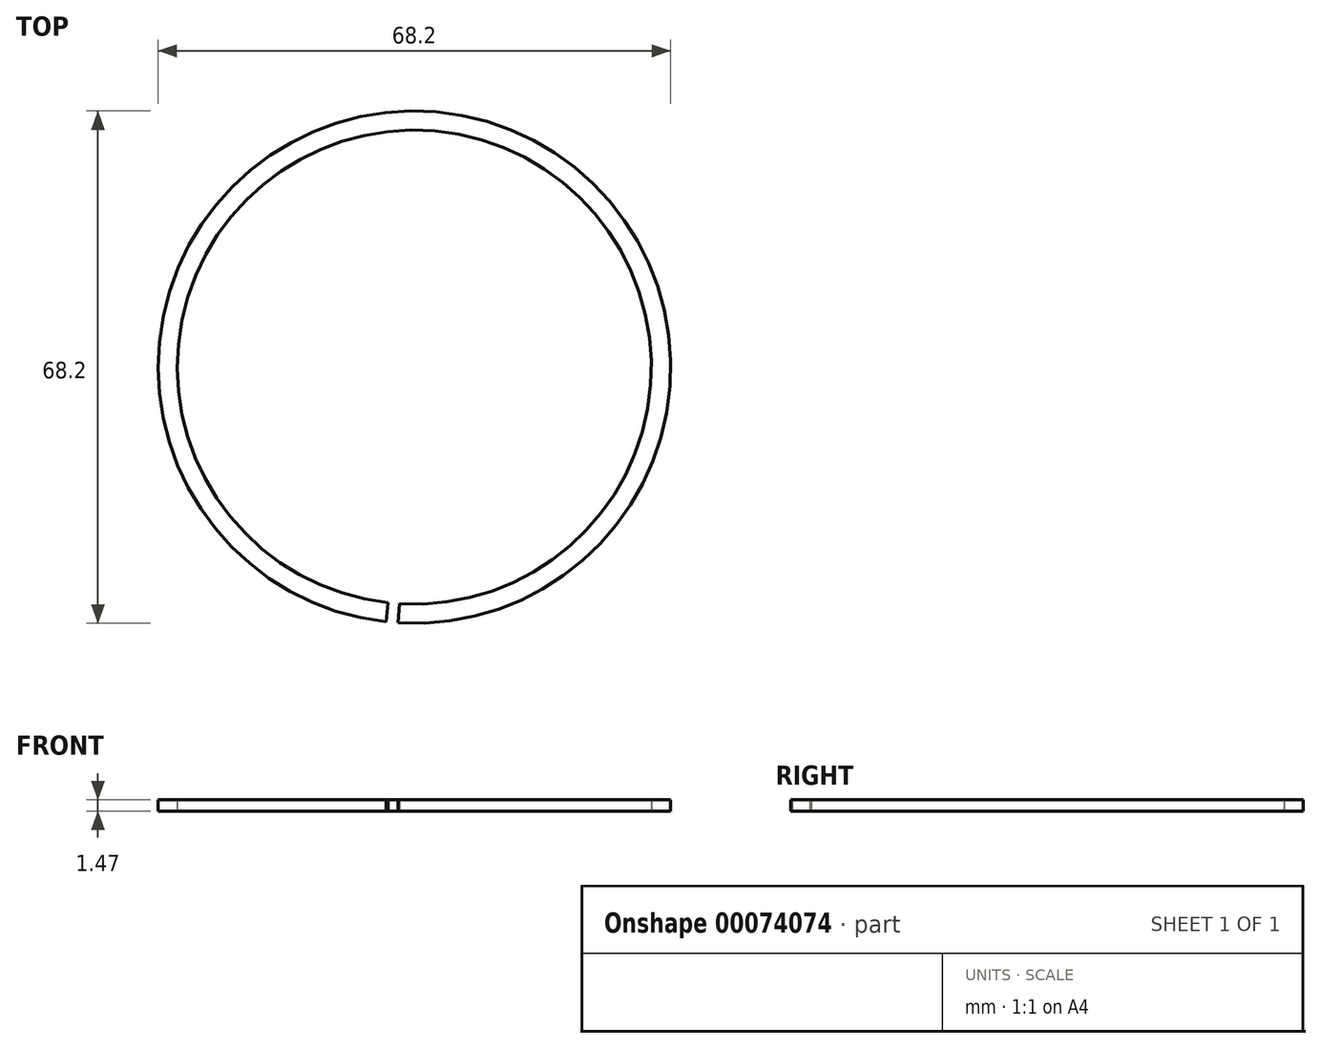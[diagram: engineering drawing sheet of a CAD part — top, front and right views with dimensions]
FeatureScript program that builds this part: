
annotation { "Feature Type Name" : "Feature", "Feature Type Description" : "" }
export const myFeature = defineFeature(function(context is Context, id is Id, definition is map)
    precondition{}
    {
        {
            var Q0;
            Q0=qCreatedBy(makeId("Top.planeOp"),FACE);
            var sketch = newSketch(context, id + "F0", { "sketchPlane" : qUnion([Q0])});
            skArc(sketch, "E0", {"start": v(-2.15, -34.03) * mm, "mid": v(2.95, 33.97) * mm, "end": v(-3.74, -33.9) * mm});
            skArc(sketch, "E1", {"start": v(-2, -31.48) * mm, "mid": v(2.73, 31.43) * mm, "end": v(-3.46, -31.36) * mm});
            skLineSegment(sketch, "E2", {"start": v(-3.46, -31.36) * mm, "end": v(-3.74, -33.9) * mm});
            skLineSegment(sketch, "E3", {"start": v(-2, -31.48) * mm, "end": v(-2.15, -34.03) * mm});
            skPoint(sketch, "E4.orphan", {"position": v(-2.25, -35.48) * mm});
            skSolve(sketch);
        }
        {
            var Q0;
            Q0=makeQuery(id+"F0.imprint","IMPRINT",FACE,{"disambiguationData":[TD([[makeQuery(id+"F0.imprint","IMPRINT",EDGE,{"derivedFrom":sQuery(id+"F0.wireOp",EDGE,"E0")}),1.0]])]});
            extrude(context, id + "F1", {"entities" : qUnion([Q0]), "depth" : 1.47 * mm});
        }
    });
